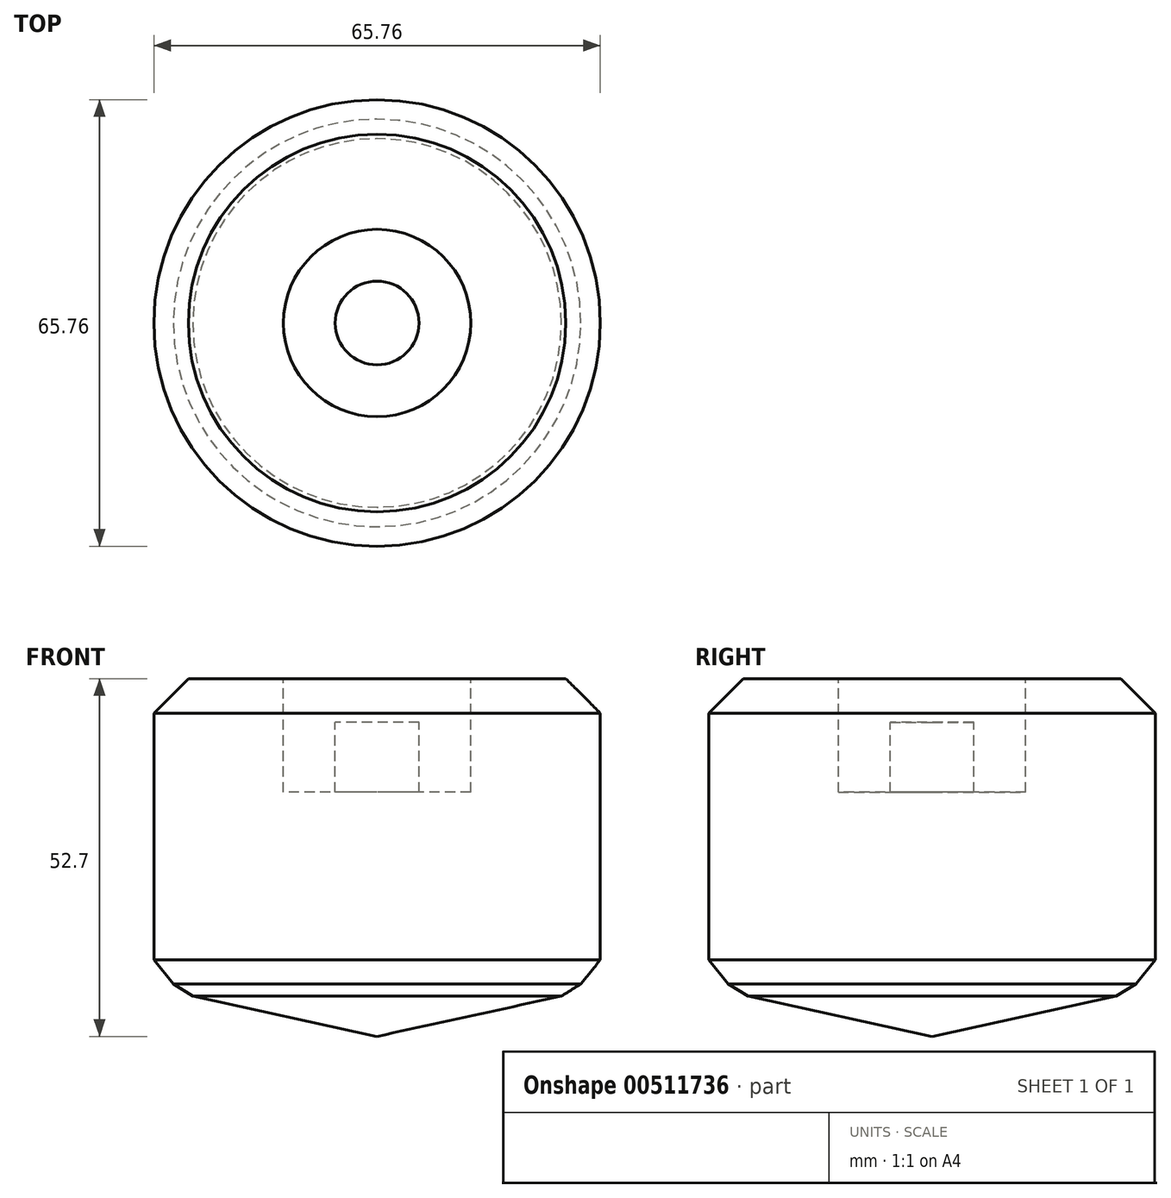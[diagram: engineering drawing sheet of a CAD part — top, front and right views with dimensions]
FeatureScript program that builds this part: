
annotation { "Feature Type Name" : "Feature", "Feature Type Description" : "" }
export const myFeature = defineFeature(function(context is Context, id is Id, definition is map)
    precondition{}
    {
        {
            var Q0;
            Q0=qCreatedBy(makeId("Front.planeOp"),FACE);
            var sketch = newSketch(context, id + "F0", { "sketchPlane" : qUnion([Q0])});
            skLineSegment(sketch, "E0.bottom", {"start": v(13.8, 52.7) * mm, "end": v(32.88, 52.7) * mm});
            skLineSegment(sketch, "E1", {"start": v(13.8, 52.7) * mm, "end": v(13.8, 35.97) * mm});
            skLineSegment(sketch, "E2", {"start": v(13.8, 35.97) * mm, "end": v(6.17, 35.97) * mm});
            skPoint(sketch, "E0.left.start.orphan", {"position": v(0, 52.7) * mm});
            skLineSegment(sketch, "E3", {"start": v(6.17, 35.97) * mm, "end": v(6.17, 46.24) * mm});
            skLineSegment(sketch, "E4", {"start": v(6.17, 46.24) * mm, "end": v(0, 46.24) * mm});
            skLineSegment(sketch, "E5", {"start": v(0, 46.24) * mm, "end": v(0, 0) * mm});
            skLineSegment(sketch, "E6", {"start": v(32.88, 52.7) * mm, "end": v(32.88, 7.2) * mm});
            skLineSegment(sketch, "E7", {"start": v(0, 0) * mm, "end": v(32.88, 7.2) * mm});
            skPoint(sketch, "E8.start.orphan", {"position": v(32.88, 0) * mm});
            skSolve(sketch);
        }
        {
            var Q0;
            Q0=makeQuery(id+"F0.imprint","IMPRINT",FACE,{"disambiguationData":[TD([[makeQuery(id+"F0.imprint","IMPRINT",EDGE,{"derivedFrom":sQuery(id+"F0.wireOp",EDGE,"E0.bottom")}),-1.0]])]});
            var Q1;
            Q1=sQuery(id+"F0.wireOp",EDGE,"E5");
            revolve(context, id + "F1", {"entities" : qUnion([Q0]), "axis" : qUnion([Q1]), "revolveType" : RevolveType.FULL});
        }
        {
            var Q0;
            Q0=makeQuery(id+"F1.opRevolve","SWEPT_FACE",FACE,{"disambiguationData":[OSD([sQuery(id+"F0.wireOp",EDGE,"E6")])]});
            chamfer(context, id + "F2", {"entities" : qUnion([Q0]), "width" : 5.08 * mm, "tangentPropagation" : true});
        }
        {
            var Q0;
            Q0=makeQuery(id+"F1.opRevolve","SWEPT_FACE",FACE,{"disambiguationData":[OSD([sQuery(id+"F0.wireOp",EDGE,"E7")])]});
            chamfer(context, id + "F3", {"entities" : qUnion([Q0]), "width" : 5.08 * mm, "tangentPropagation" : true});
        }
    });
